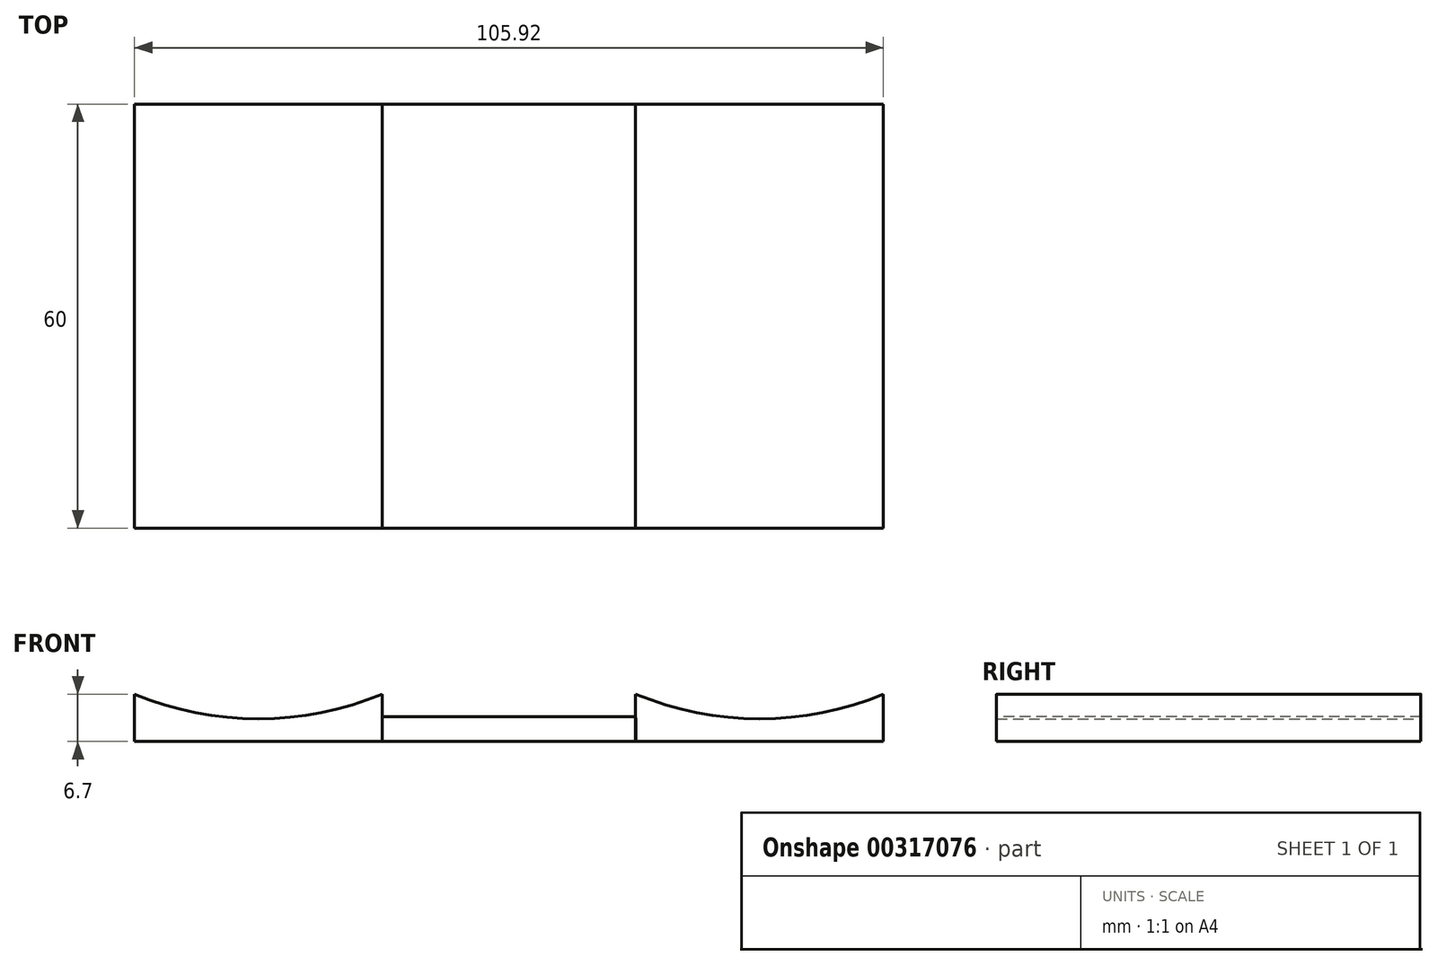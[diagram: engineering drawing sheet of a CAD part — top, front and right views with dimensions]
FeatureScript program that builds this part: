
annotation { "Feature Type Name" : "Feature", "Feature Type Description" : "" }
export const myFeature = defineFeature(function(context is Context, id is Id, definition is map)
    precondition{}
    {
        {
            var Q0;
            Q0=qCreatedBy(makeId("Front.planeOp"),FACE);
            var sketch = newSketch(context, id + "F0", { "sketchPlane" : qUnion([Q0])});
            skLineSegment(sketch, "E0.MirrorCS", {"start": v(17.9, 3.2) * mm, "end": v(17.96, -3.5) * mm});
            skLineSegment(sketch, "E1.MirrorCS", {"start": v(52.96, -3.5) * mm, "end": v(17.96, -3.5) * mm});
            skPoint(sketch, "E2.MirrorP", {"position": v(35.46, -0.3) * mm});
            skLineSegment(sketch, "E3.MirrorCS", {"start": v(52.96, 3.18) * mm, "end": v(52.96, -3.5) * mm});
            skArc(sketch, "E4", {"start": v(17.9, 3.2) * mm, "mid": v(35.43, -0.3) * mm, "end": v(52.96, 3.18) * mm});
            skLineSegment(sketch, "E5.MirrorCS", {"start": v(-17.9, 3.2) * mm, "end": v(-17.96, -3.5) * mm});
            skPoint(sketch, "E6.MirrorP", {"position": v(-35.46, -0.3) * mm});
            skLineSegment(sketch, "E7.MirrorCS", {"start": v(-52.96, -3.5) * mm, "end": v(-17.96, -3.5) * mm});
            skLineSegment(sketch, "E8.MirrorCS", {"start": v(-52.96, 3.18) * mm, "end": v(-52.96, -3.5) * mm});
            skArc(sketch, "E9.MirrorCS", {"start": v(-17.9, 3.2) * mm, "mid": v(-35.43, -0.3) * mm, "end": v(-52.96, 3.18) * mm});
            skSolve(sketch);
        }
        {
            var Q0;
            Q0=makeQuery(id+"F0.imprint","IMPRINT",FACE,{"disambiguationData":[TD([[makeQuery(id+"F0.imprint","IMPRINT",EDGE,{"derivedFrom":sQuery(id+"F0.wireOp",EDGE,"E5.MirrorCS")}),-1.0]])]});
            var Q1;
            Q1=makeQuery(id+"F0.imprint","IMPRINT",FACE,{"disambiguationData":[TD([[makeQuery(id+"F0.imprint","IMPRINT",EDGE,{"derivedFrom":sQuery(id+"F0.wireOp",EDGE,"E0.MirrorCS")}),1.0]])]});
            extrude(context, id + "F1", {"entities" : qUnion([Q0, Q1]), "depth" : 60 * mm, "offsetDistance" : 25 * mm});
        }
        {
            var Q0;
            Q0=qCreatedBy(makeId("Top.planeOp"),FACE);
            var sketch = newSketch(context, id + "F2", { "sketchPlane" : qUnion([Q0])});
            skLineSegment(sketch, "E10.bottom", {"start": v(-17.92, 0) * mm, "end": v(17.88, 0) * mm});
            skLineSegment(sketch, "E10.top", {"start": v(-17.92, -60) * mm, "end": v(17.88, -60) * mm});
            skLineSegment(sketch, "E10.left", {"start": v(-17.92, 0) * mm, "end": v(-17.92, -60) * mm});
            skLineSegment(sketch, "E10.right", {"start": v(17.88, 0) * mm, "end": v(17.88, -60) * mm});
            skSolve(sketch);
        }
        {
            var Q0;
            Q0=makeQuery(id+"F2.imprint","IMPRINT",FACE,{"disambiguationData":[TD([[makeQuery(id+"F2.imprint","IMPRINT",EDGE,{"derivedFrom":sQuery(id+"F2.wireOp",EDGE,"E10.bottom")}),-1.0]])]});
            extrude(context, id + "F3", {"entities" : qUnion([Q0]), "operationType" : NewBodyOperationType.ADD, "oppositeDirection" : true, "depth" : 3.5 * mm, "offsetDistance" : 25 * mm});
        }
    });
